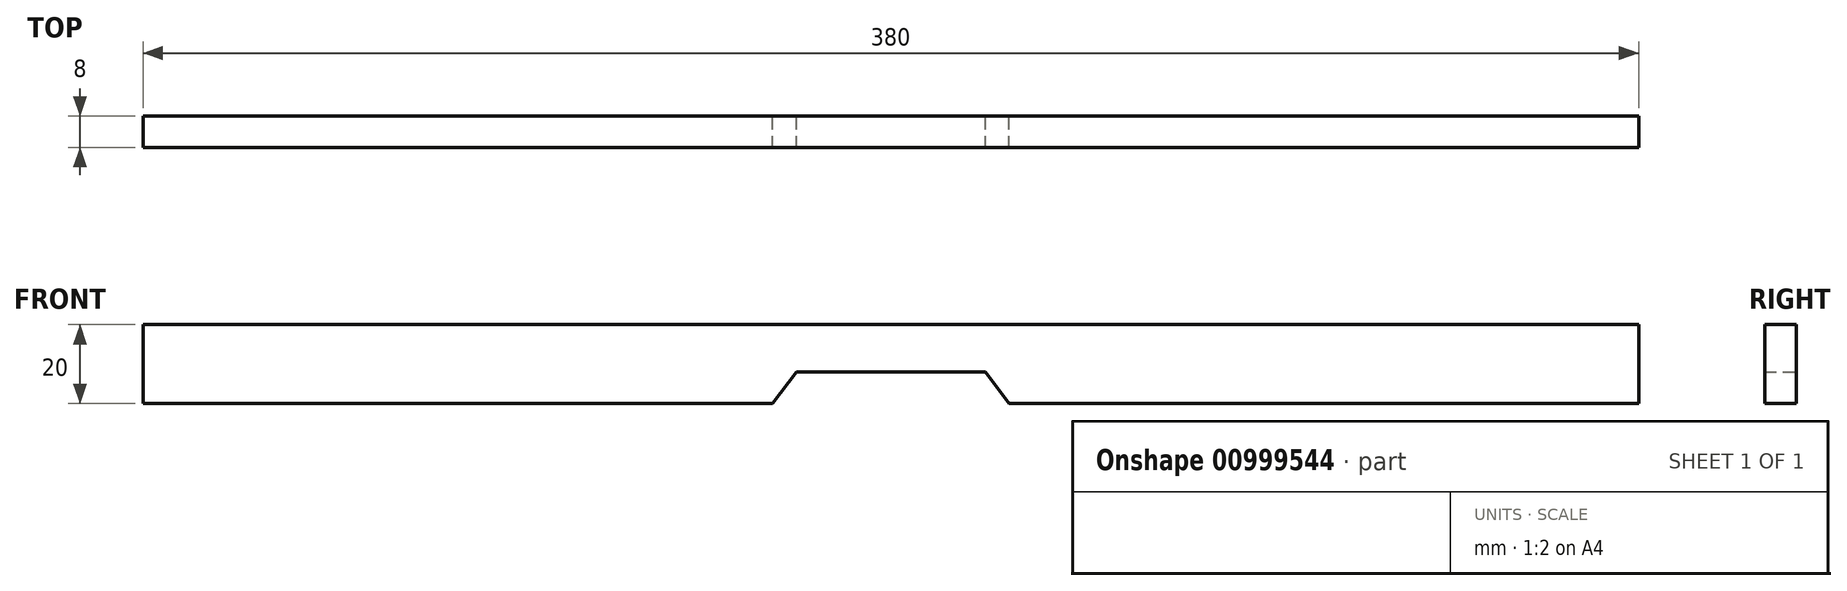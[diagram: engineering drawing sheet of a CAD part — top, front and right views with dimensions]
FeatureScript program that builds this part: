
annotation { "Feature Type Name" : "Feature", "Feature Type Description" : "" }
export const myFeature = defineFeature(function(context is Context, id is Id, definition is map)
    precondition{}
    {
        {
            var Q0;
            Q0=qCreatedBy(makeId("Front.planeOp"),FACE);
            var sketch = newSketch(context, id + "F0", { "sketchPlane" : qUnion([Q0]), "disableImprinting" : false});
            skLineSegment(sketch, "E0.bottom", {"start": v(-190, 10) * mm, "end": v(190, 10) * mm});
            skLineSegment(sketch, "E0.top", {"start": v(-190, -10) * mm, "end": v(-30, -10) * mm});
            skLineSegment(sketch, "E0.left", {"start": v(-190, 10) * mm, "end": v(-190, -10) * mm});
            skLineSegment(sketch, "E0.right", {"start": v(190, 10) * mm, "end": v(190, -10) * mm});
            skPoint(sketch, "E0.middle", {"position": v(0, 0) * mm});
            skPoint(sketch, "E1", {"position": v(-30, -10) * mm});
            skPoint(sketch, "E2", {"position": v(30, -10) * mm});
            skPoint(sketch, "E3", {"position": v(-24, -2) * mm});
            skPoint(sketch, "E4", {"position": v(24, -2) * mm});
            skLineSegment(sketch, "E5", {"start": v(-30, -10) * mm, "end": v(-24, -2) * mm});
            skLineSegment(sketch, "E6", {"start": v(-24, -2) * mm, "end": v(24, -2) * mm});
            skLineSegment(sketch, "E7", {"start": v(24, -2) * mm, "end": v(30, -10) * mm});
            skLineSegment(sketch, "E8.trimOffspring", {"start": v(30, -10) * mm, "end": v(190, -10) * mm});
            skSolve(sketch);
        }
        {
            var Q0;
            Q0=makeQuery(id+"F0.imprint","IMPRINT",FACE,{"disambiguationData":[TD([[makeQuery(id+"F0.imprint","IMPRINT",EDGE,{"derivedFrom":sQuery(id+"F0.wireOp",EDGE,"E0.bottom")}),-1.0]])]});
            extrude(context, id + "F1", {"entities" : qUnion([Q0]), "flatOperationType" : FlatOperationType.REMOVE, "thickness1" : 5 * mm, "thickness2" : 0 * mm, "thickness" : 5 * mm, "depth" : 8 * mm, "offsetDistance" : 25 * mm, "startOffsetBound" : StartOffsetType.BLIND, "startOffsetDistance" : 25 * mm, "domain" : OperationDomain.MODEL});
        }
    });
